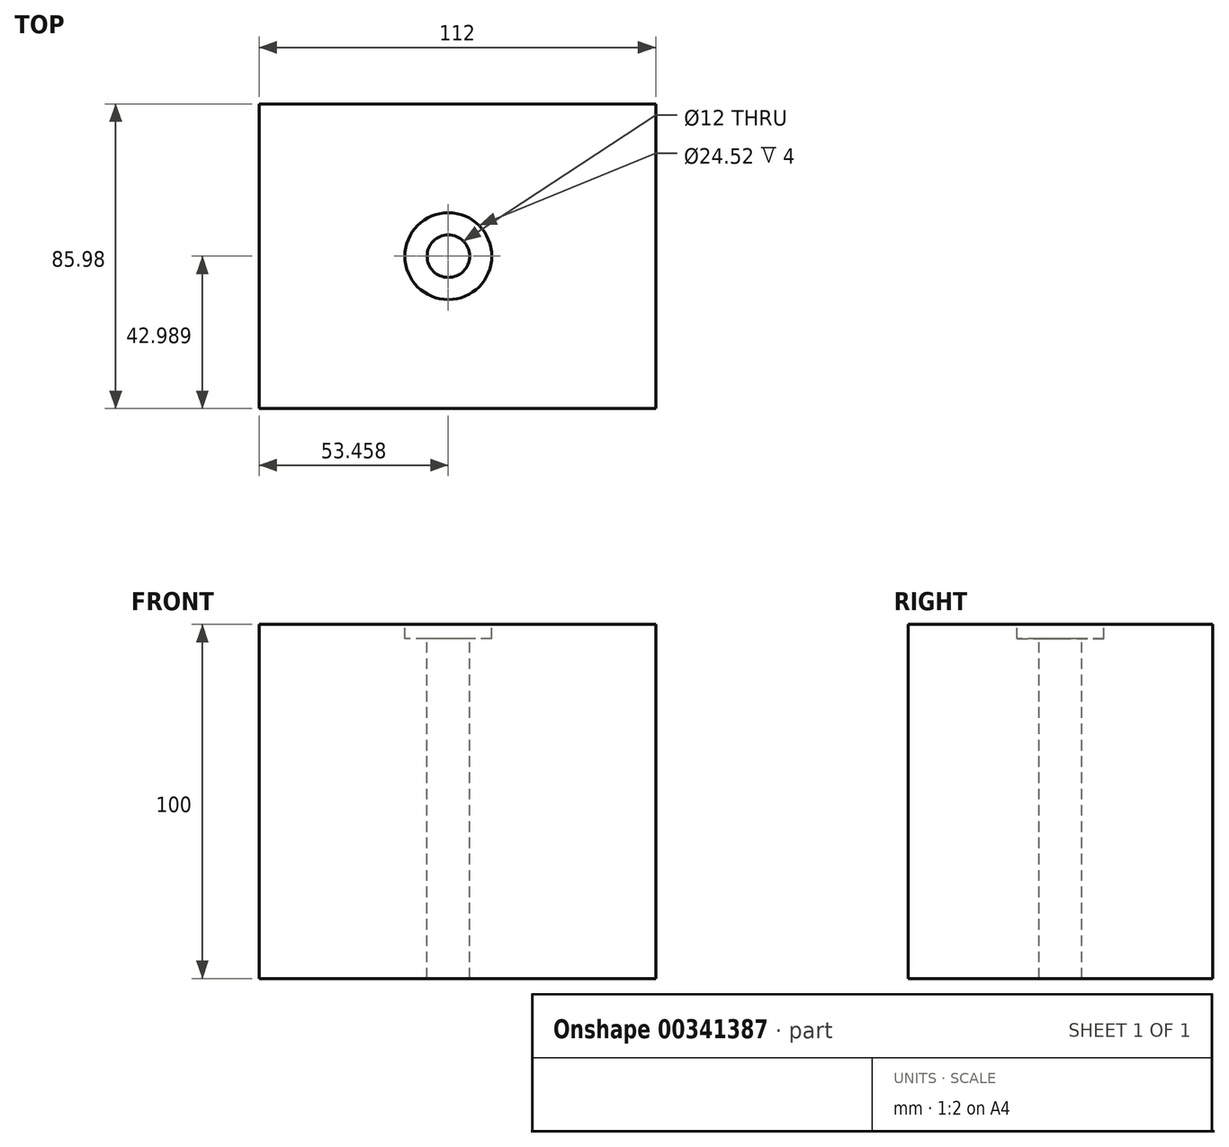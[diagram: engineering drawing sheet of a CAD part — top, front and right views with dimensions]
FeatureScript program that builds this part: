
annotation { "Feature Type Name" : "Feature", "Feature Type Description" : "" }
export const myFeature = defineFeature(function(context is Context, id is Id, definition is map)
    precondition{}
    {
        {
            var Q0;
            Q0=qCreatedBy(makeId("Top.planeOp"),FACE);
            var sketch = newSketch(context, id + "F0", { "sketchPlane" : qUnion([Q0])});
            skLineSegment(sketch, "E0.bottom", {"start": v(-44.03, 24.68) * mm, "end": v(67.97, 24.68) * mm});
            skLineSegment(sketch, "E0.top", {"start": v(-44.03, -61.3) * mm, "end": v(67.97, -61.3) * mm});
            skLineSegment(sketch, "E0.left", {"start": v(-44.03, 24.68) * mm, "end": v(-44.03, -61.3) * mm});
            skLineSegment(sketch, "E0.right", {"start": v(67.97, 24.68) * mm, "end": v(67.97, -61.3) * mm});
            skSolve(sketch);
        }
        {
            var Q0;
            Q0 = qSketchRegion(id + "F0", true);
            extrude(context, id + "F1", {"entities" : qUnion([Q0]), "depth" : 100 * mm});
        }
        {
            var Q0;
            Q0=makeQuery(id+"F1.opExtrude","CAP_FACE",FACE,{"disambiguationData":[OSD([sQuery(id+"F0.wireOp",EDGE,"E0.bottom"),sQuery(id+"F0.wireOp",EDGE,"E0.top"),sQuery(id+"F0.wireOp",EDGE,"E0.left"),sQuery(id+"F0.wireOp",EDGE,"E0.right")])],"isStart":false});
            var sketch = newSketch(context, id + "F2", { "sketchPlane" : qUnion([Q0])});
            skCircle(sketch, "E1", {"center": v(9.43, -18.31) * mm, "radius": 11.04 * mm});
            skPoint(sketch, "E1.centerSnap0", {"position": v(-44.03, -18.31) * mm});
            skSolve(sketch);
        }
        {
            var Q0;
            Q0=sQuery(id+"F2.wireOp",VERTEX,"E1.center");
            var Q1;
            Q1=makeQuery(id+"F1.opExtrude","SWEPT_BODY",BODY,{"disambiguationData":[OSD([sQuery(id+"F0.wireOp",EDGE,"E0.bottom"),sQuery(id+"F0.wireOp",EDGE,"E0.top"),sQuery(id+"F0.wireOp",EDGE,"E0.left"),sQuery(id+"F0.wireOp",EDGE,"E0.right")])]});
            hole(context, id + "F3", {"style" : HoleStyle.SIMPLE, "endStyle" : HoleEndStyle.THROUGH, "holeDiameter" : 12 * mm, "tappedDepth" : 12.7 * mm, "tapClearance" : 3, "locations" : qUnion([Q0]), "scope" : qUnion([Q1])});
        }
        {
            var Q0;
            Q0=makeQuery(id+"F1.opExtrude","CAP_FACE",FACE,{"disambiguationData":[OSD([sQuery(id+"F0.wireOp",EDGE,"E0.bottom"),sQuery(id+"F0.wireOp",EDGE,"E0.top"),sQuery(id+"F0.wireOp",EDGE,"E0.left"),sQuery(id+"F0.wireOp",EDGE,"E0.right")])],"isStart":false});
            var sketch = newSketch(context, id + "F4", { "sketchPlane" : qUnion([Q0])});
            skCircle(sketch, "E2", {"center": v(9.43, -18.31) * mm, "radius": 12.26 * mm});
            skSolve(sketch);
        }
        {
            var Q0;
            Q0 = qSketchRegion(id + "F4", true);
            extrude(context, id + "F5", {"entities" : qUnion([Q0]), "operationType" : NewBodyOperationType.REMOVE, "oppositeDirection" : true, "depth" : 4 * mm});
        }
    });
